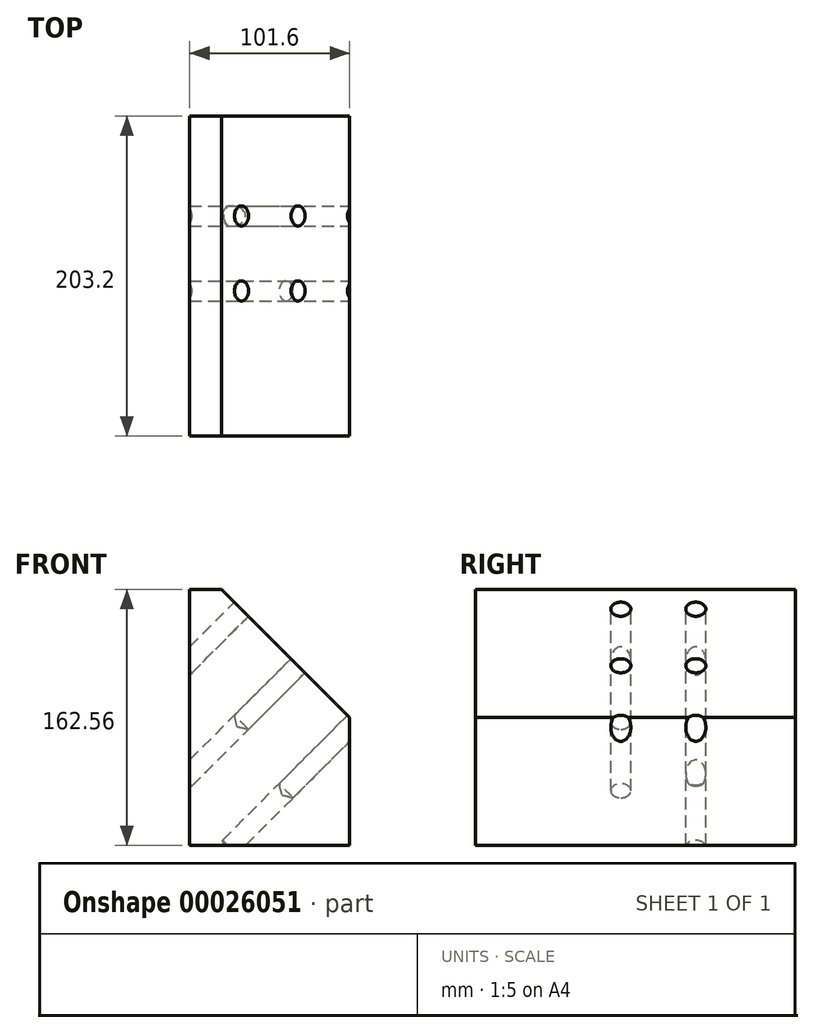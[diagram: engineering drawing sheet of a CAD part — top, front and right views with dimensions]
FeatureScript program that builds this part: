
annotation { "Feature Type Name" : "Feature", "Feature Type Description" : "" }
export const myFeature = defineFeature(function(context is Context, id is Id, definition is map)
    precondition{}
    {
        {
            var Q0;
            Q0=qCreatedBy(makeId("Right.planeOp"),FACE);
            var sketch = newSketch(context, id + "F0", { "sketchPlane" : qUnion([Q0])});
            skLineSegment(sketch, "E0.rect.bottom", {"start": v(-101.6, 81.28) * mm, "end": v(101.6, 81.28) * mm});
            skLineSegment(sketch, "E0.rect.top", {"start": v(-101.6, -81.28) * mm, "end": v(101.6, -81.28) * mm});
            skLineSegment(sketch, "E0.rect.left", {"start": v(-101.6, 81.28) * mm, "end": v(-101.6, -81.28) * mm});
            skLineSegment(sketch, "E0.rect.right", {"start": v(101.6, 81.28) * mm, "end": v(101.6, -81.28) * mm});
            skPoint(sketch, "E0.rect.middle", {"position": v(0, 0) * mm});
            skSolve(sketch);
        }
        {
            var Q0;
            Q0=makeQuery(id+"F0.imprint","IMPRINT",FACE,{"disambiguationData":[TD([[makeQuery(id+"F0.imprint","IMPRINT",EDGE,{"derivedFrom":sQuery(id+"F0.wireOp",EDGE,"E0.rect.bottom")}),-1.0]])]});
            extrude(context, id + "F1", {"entities" : qUnion([Q0]), "depth" : 101.6 * mm});
        }
        {
            var Q0;
            Q0=makeQuery(id+"F1.opExtrude","CAP_EDGE",EDGE,{"disambiguationData":[OSD([sQuery(id+"F0.wireOp",EDGE,"E0.rect.bottom")])],"isStart":false});
            chamfer(context, id + "F2", {"entities" : qUnion([Q0]), "width" : 81.28 * mm, "tangentPropagation" : true});
        }
        {
            var Q0;
            Q0=makeQuery(id+"F2.opChamfer","BLEND_FACE",FACE,{"disambiguationData":[OSD([sQuery(id+"F0.wireOp",EDGE,"E0.rect.bottom")])]});
            var sketch = newSketch(context, id + "F3", { "sketchPlane" : qUnion([Q0])});
            skCircle(sketch, "E1", {"center": v(-9.44, -76.2) * mm, "radius": 6.35 * mm});
            skCircle(sketch, "E2", {"center": v(-9.44, -25.4) * mm, "radius": 6.35 * mm});
            skCircle(sketch, "E3", {"center": v(-9.44, 25.4) * mm, "radius": 6.35 * mm});
            skCircle(sketch, "E4", {"center": v(-9.44, 76.2) * mm, "radius": 6.35 * mm});
            skCircle(sketch, "E5", {"center": v(38.17, -76.2) * mm, "radius": 6.35 * mm});
            skCircle(sketch, "E6", {"center": v(38.17, -25.4) * mm, "radius": 6.35 * mm});
            skCircle(sketch, "E7", {"center": v(38.17, 25.4) * mm, "radius": 6.35 * mm});
            skCircle(sketch, "E8", {"center": v(38.17, 76.2) * mm, "radius": 6.35 * mm});
            skCircle(sketch, "E9", {"center": v(38.17, -76.2) * mm, "radius": 6.33 * mm});
            skCircle(sketch, "E10", {"center": v(38.17, -25.4) * mm, "radius": 6.55 * mm});
            skCircle(sketch, "E11", {"center": v(38.17, 25.4) * mm, "radius": 6.38 * mm});
            skCircle(sketch, "E12", {"center": v(38.17, 76.2) * mm, "radius": 6.12 * mm});
            skSolve(sketch);
        }
        {
            var Q0;
            Q0=sQuery(id+"F3.wireOp",VERTEX,"E1.center");
            var Q1;
            Q1=sQuery(id+"F3.wireOp",VERTEX,"E2.center");
            var Q2;
            Q2=sQuery(id+"F3.wireOp",VERTEX,"E3.center");
            var Q3;
            Q3=sQuery(id+"F3.wireOp",VERTEX,"E4.center");
            var Q4;
            Q4=makeQuery(id+"F1.opExtrude","SWEPT_BODY",BODY,{"disambiguationData":[OSD([sQuery(id+"F0.wireOp",EDGE,"E0.rect.bottom"),sQuery(id+"F0.wireOp",EDGE,"E0.rect.top"),sQuery(id+"F0.wireOp",EDGE,"E0.rect.left"),sQuery(id+"F0.wireOp",EDGE,"E0.rect.right")])]});
            hole(context, id + "F4", {"style" : HoleStyle.SIMPLE, "holeDiameter" : 12.7 * mm, "endStyle" : HoleEndStyle.BLIND, "holeDepth" : 50.8 * mm, "locations" : qUnion([Q0, Q1, Q2, Q3]), "scope" : qUnion([Q4])});
        }
        {
            var Q0;
            Q0=makeQuery(id+"F2.opChamfer","BLEND_FACE",FACE,{"disambiguationData":[OSD([sQuery(id+"F0.wireOp",EDGE,"E0.rect.bottom")])]});
            var sketch = newSketch(context, id + "F5", { "sketchPlane" : qUnion([Q0])});
            skCircle(sketch, "E13", {"center": v(38.17, -76.2) * mm, "radius": 6.35 * mm});
            skCircle(sketch, "E14", {"center": v(38.17, -25.4) * mm, "radius": 6.35 * mm});
            skCircle(sketch, "E15", {"center": v(38.17, 25.4) * mm, "radius": 6.35 * mm});
            skCircle(sketch, "E16", {"center": v(38.17, 76.2) * mm, "radius": 6.35 * mm});
            skSolve(sketch);
        }
        {
            var Q0;
            Q0=sQuery(id+"F5.wireOp",VERTEX,"E13.center");
            var Q1;
            Q1=sQuery(id+"F5.wireOp",VERTEX,"E14.center");
            var Q2;
            Q2=sQuery(id+"F5.wireOp",VERTEX,"E15.center");
            var Q3;
            Q3=sQuery(id+"F5.wireOp",VERTEX,"E16.center");
            var Q4;
            Q4=makeQuery(id+"F1.opExtrude","SWEPT_BODY",BODY,{"disambiguationData":[OSD([sQuery(id+"F0.wireOp",EDGE,"E0.rect.bottom"),sQuery(id+"F0.wireOp",EDGE,"E0.rect.top"),sQuery(id+"F0.wireOp",EDGE,"E0.rect.left"),sQuery(id+"F0.wireOp",EDGE,"E0.rect.right")])]});
            hole(context, id + "F6", {"style" : HoleStyle.SIMPLE, "holeDiameter" : 12.7 * mm, "endStyle" : HoleEndStyle.BLIND, "holeDepth" : 101.6 * mm, "locations" : qUnion([Q0, Q1, Q2, Q3]), "scope" : qUnion([Q4])});
        }
    });
